# Revit family: CENTUM Direktanschluss
name_source: partatom
category: HLS-Bauteile
revit_build: Autodesk Revit 2017 (Build: 20190507_1515(x64)
units: mm (PartAtom-declared; Revit-internal decimal feet)

## family parameters
Arbeitsebenenbasiert = Ja
Beim Laden mit Abzugskörper schneiden = Nein
Bemaßung runder Anschluss = Durchmesser verwenden
Gemeinsam genutzt = Ja
Immer vertikal = Nein
Raumberechnungspunkt = Nein
Teiletyp = Normal

## types (2) — shared parameters
Fabrikat = MEFA
Firma = MEFA Befestigungs- und Montagesysteme GmbH
Gewicht = 0.07 kg
Gewicht pro Bauteil = 0.07 kg
Höhe Bundmutter = 25 mm
Kurztext1 = Direktanschluss CENTUM
Material = Stahl
Mengeneinheit = St
Oberflaeche = Zink-Nickel
Profil = CENTUM
Profiltyp = XL 80, XL 100, XL 120, XL 200
Schlüsselweite = 17
Vorgabe-Ansicht = 1219 mm
max. zul. Last = 3.00 kN
vpe = 50 St

## per-type parameters (varying)
| type | Artikelnummer | Bundmutter | EAN | Gewinde | Kurztext2 |
| CENTUM Direktanschluss M12 | 1640016012 | Bundmutter CENTUM : Bundmutter M12 | 4250928450517 | M12 | M12 |
| CENTUM Direktanschluss M10 | 1640016010 | Bundmutter CENTUM : Bundmutter M10 | 4250928450500 | M10 | M10 |

## geometry (parser evidence)
native form markers: Sweep x3
no freeform markers — native parametric forms only
